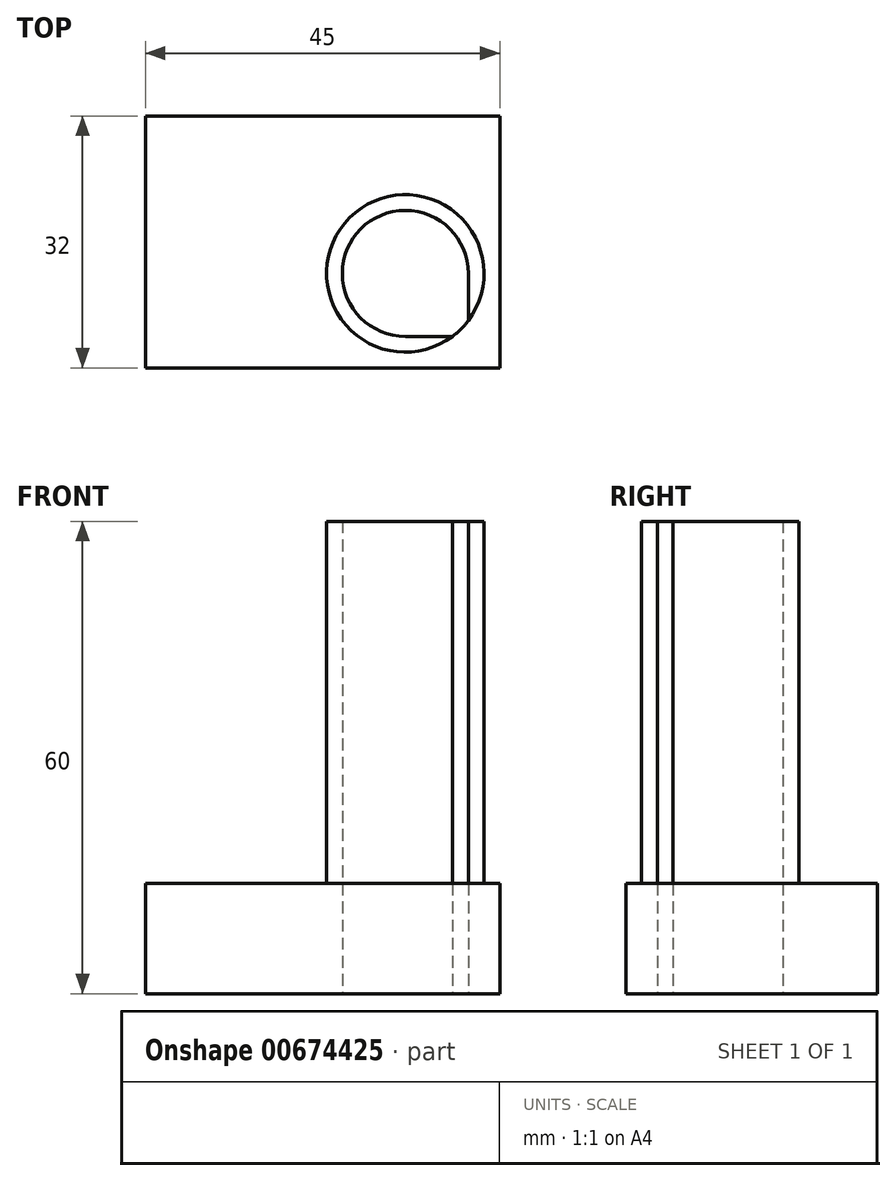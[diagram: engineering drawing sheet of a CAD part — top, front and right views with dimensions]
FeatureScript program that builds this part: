
annotation { "Feature Type Name" : "Feature", "Feature Type Description" : "" }
export const myFeature = defineFeature(function(context is Context, id is Id, definition is map)
    precondition{}
    {
        {
            var Q0;
            Q0=qCreatedBy(makeId("Top.planeOp"),FACE);
            var sketch = newSketch(context, id + "F0", { "sketchPlane" : qUnion([Q0])});
            skLineSegment(sketch, "E0.bottom", {"start": v(0, 0) * mm, "end": v(45, 0) * mm});
            skLineSegment(sketch, "E0.top", {"start": v(0, 32) * mm, "end": v(45, 32) * mm});
            skLineSegment(sketch, "E0.left", {"start": v(0, 0) * mm, "end": v(0, 32) * mm});
            skLineSegment(sketch, "E0.right", {"start": v(45, 0) * mm, "end": v(45, 32) * mm});
            skLineSegment(sketch, "E1.0", {"start": v(2, 2) * mm, "end": v(2, 30) * mm});
            skLineSegment(sketch, "E1.1", {"start": v(2, 2) * mm, "end": v(43, 2) * mm});
            skLineSegment(sketch, "E1.2", {"start": v(43, 2) * mm, "end": v(43, 30) * mm});
            skLineSegment(sketch, "E1.3", {"start": v(2, 30) * mm, "end": v(43, 30) * mm});
            skLineSegment(sketch, "E2.0", {"start": v(41, 4) * mm, "end": v(41, 30) * mm});
            skLineSegment(sketch, "E2.1", {"start": v(2, 4) * mm, "end": v(41, 4) * mm});
            skLineSegment(sketch, "E3.0", {"start": v(46, 4) * mm, "end": v(46, 30) * mm});
            skLineSegment(sketch, "E4", {"start": v(33, 4) * mm, "end": v(33, 30) * mm});
            skLineSegment(sketch, "E5", {"start": v(41, 12) * mm, "end": v(2, 12) * mm});
            skCircle(sketch, "E6", {"center": v(33, 12) * mm, "radius": 8 * mm});
            skCircle(sketch, "E7.0", {"center": v(33, 12) * mm, "radius": 10 * mm});
            skLineSegment(sketch, "E8", {"start": v(0, 14) * mm, "end": v(45, 14) * mm});
            skSolve(sketch);
        }
        {
            var Q0;
            Q0=makeQuery(id+"F0.imprint","IMPRINT",FACE,{"disambiguationData":[TD([[makeQuery(id+"F0.imprint","IMPRINT",EDGE,{"derivedFrom":sQuery(id+"F0.wireOp",EDGE,"E0.bottom")}),1.0]])]});
            var Q1;
            {var subQ1=sQuery(id+"F0.wireOp",EDGE,"E1.3");var subQ5=sQuery(id+"F0.wireOp",EDGE,"E1.0");var subQ6=makeQuery(id+"F0.imprint","INTERSECT",VERTEX,{"derivedFrom":[subQ5,subQ1]});Q1=makeQuery(id+"F0.imprint","IMPRINT",FACE,{"disambiguationData":[TD([[makeQuery(id+"F0.imprint","IMPRINT",EDGE,{"disambiguationData":[TD([[subQ6,1.0]])],"derivedFrom":subQ5}),-1.0]])]});}
            var Q2;
            {var subQ0=sQuery(id+"F0.wireOp",EDGE,"E2.0");var subQ1=sQuery(id+"F0.wireOp",EDGE,"E1.3");var subQ2=makeQuery(id+"F0.imprint","INTERSECT",VERTEX,{"derivedFrom":[subQ1,subQ0]});Q2=makeQuery(id+"F0.imprint","IMPRINT",FACE,{"disambiguationData":[TD([[makeQuery(id+"F0.imprint","IMPRINT",EDGE,{"disambiguationData":[TD([[subQ2,1.0]])],"derivedFrom":subQ1}),-1.0]])]});}
            var Q3;
            {var subQ0=sQuery(id+"F0.wireOp",EDGE,"E2.1");var subQ1=sQuery(id+"F0.wireOp",EDGE,"E1.0");var subQ2=makeQuery(id+"F0.imprint","INTERSECT",VERTEX,{"derivedFrom":[subQ1,subQ0]});Q3=makeQuery(id+"F0.imprint","IMPRINT",FACE,{"disambiguationData":[TD([[makeQuery(id+"F0.imprint","IMPRINT",EDGE,{"disambiguationData":[TD([[subQ2,-1.0]])],"derivedFrom":subQ1}),-1.0]])]});}
            var Q4;
            {var subQ4=sQuery(id+"F0.wireOp",EDGE,"E1.1");Q4=makeQuery(id+"F0.imprint","IMPRINT",FACE,{"disambiguationData":[TD([[makeQuery(id+"F0.imprint","IMPRINT",EDGE,{"derivedFrom":subQ4}),1.0]])]});}
            var Q5;
            {var subQ0=sQuery(id+"F0.wireOp",EDGE,"E2.1");var subQ1=sQuery(id+"F0.wireOp",EDGE,"E2.0");var subQ2=makeQuery(id+"F0.imprint","INTERSECT",VERTEX,{"derivedFrom":[subQ1,subQ0]});Q5=makeQuery(id+"F0.imprint","IMPRINT",FACE,{"disambiguationData":[TD([[makeQuery(id+"F0.imprint","IMPRINT",EDGE,{"disambiguationData":[TD([[subQ2,-1.0]])],"derivedFrom":subQ1}),1.0]])]});}
            var Q6;
            {var subQ0=sQuery(id+"F0.wireOp",EDGE,"E6");var subQ5=sQuery(id+"F0.wireOp",EDGE,"E5");var subQ6=makeQuery(id+"F0.imprint","INTERSECT",VERTEX,{"derivedFrom":[subQ5,subQ0]});Q6=makeQuery(id+"F0.imprint","IMPRINT",FACE,{"disambiguationData":[TD([[makeQuery(id+"F0.imprint","IMPRINT",EDGE,{"disambiguationData":[TD([[subQ6,-1.0]])],"derivedFrom":subQ5}),1.0]])]});}
            var Q7;
            {var subQ2=sQuery(id+"F0.wireOp",EDGE,"E7.0");var subQ4=makeQuery(id+"F0.imprint","INTERSECT",VERTEX,{"derivedFrom":[sQuery(id+"F0.wireOp",EDGE,"E1.1"),subQ2]});Q7=makeQuery(id+"F0.imprint","IMPRINT",FACE,{"disambiguationData":[TD([[makeQuery(id+"F0.imprint","IMPRINT",EDGE,{"disambiguationData":[TD([[subQ4,1.0]])],"derivedFrom":subQ2}),1.0]])]});}
            var Q8;
            {var subQ0=sQuery(id+"F0.wireOp",EDGE,"E6");var subQ1=sQuery(id+"F0.wireOp",EDGE,"E4");var subQ2=makeQuery(id+"F0.imprint","INTERSECT",VERTEX,{"derivedFrom":[subQ1,subQ0]});Q8=makeQuery(id+"F0.imprint","IMPRINT",FACE,{"disambiguationData":[TD([[makeQuery(id+"F0.imprint","IMPRINT",EDGE,{"disambiguationData":[TD([[subQ2,-1.0]])],"derivedFrom":subQ1}),1.0]])]});}
            var Q9;
            {var subQ1=sQuery(id+"F0.wireOp",EDGE,"E2.0");var subQ3=sQuery(id+"F0.wireOp",EDGE,"E7.0");var subQ4=makeQuery(id+"F0.imprint","INTERSECT",VERTEX,{"disambiguationData":[OD(0.0)],"derivedFrom":[subQ1,subQ3]});Q9=makeQuery(id+"F0.imprint","IMPRINT",FACE,{"disambiguationData":[TD([[makeQuery(id+"F0.imprint","IMPRINT",EDGE,{"disambiguationData":[TD([[subQ4,1.0]])],"derivedFrom":subQ3}),1.0]])]});}
            var Q10;
            {var subQ0=sQuery(id+"F0.wireOp",EDGE,"E6");var subQ5=sQuery(id+"F0.wireOp",EDGE,"E4");var subQ6=makeQuery(id+"F0.imprint","INTERSECT",VERTEX,{"derivedFrom":[subQ5,subQ0]});Q10=makeQuery(id+"F0.imprint","IMPRINT",FACE,{"disambiguationData":[TD([[makeQuery(id+"F0.imprint","IMPRINT",EDGE,{"disambiguationData":[TD([[subQ6,-1.0]])],"derivedFrom":subQ5}),-1.0]])]});}
            var Q11;
            {var subQ2=sQuery(id+"F0.wireOp",EDGE,"E7.0");var subQ5=makeQuery(id+"F0.imprint","INTERSECT",VERTEX,{"derivedFrom":[sQuery(id+"F0.wireOp",EDGE,"E1.2"),subQ2]});Q11=makeQuery(id+"F0.imprint","IMPRINT",FACE,{"disambiguationData":[TD([[makeQuery(id+"F0.imprint","IMPRINT",EDGE,{"disambiguationData":[TD([[subQ5,-1.0]])],"derivedFrom":subQ2}),1.0]])]});}
            var Q12;
            {var subQ6=sQuery(id+"F0.wireOp",EDGE,"E1.2");var subQ7=sQuery(id+"F0.wireOp",EDGE,"E1.1");var subQ8=makeQuery(id+"F0.imprint","INTERSECT",VERTEX,{"derivedFrom":[subQ7,subQ6]});Q12=makeQuery(id+"F0.imprint","IMPRINT",FACE,{"disambiguationData":[TD([[makeQuery(id+"F0.imprint","IMPRINT",EDGE,{"disambiguationData":[TD([[subQ8,1.0]])],"derivedFrom":subQ7}),1.0]])]});}
            var Q13;
            {var subQ0=sQuery(id+"F0.wireOp",EDGE,"E1.3");var subQ1=sQuery(id+"F0.wireOp",EDGE,"E1.2");var subQ2=makeQuery(id+"F0.imprint","INTERSECT",VERTEX,{"derivedFrom":[subQ1,subQ0]});Q13=makeQuery(id+"F0.imprint","IMPRINT",FACE,{"disambiguationData":[TD([[makeQuery(id+"F0.imprint","IMPRINT",EDGE,{"disambiguationData":[TD([[subQ2,1.0]])],"derivedFrom":subQ1}),1.0]])]});}
            var Q14;
            {var subQ0=sQuery(id+"F0.wireOp",EDGE,"E5");var subQ1=sQuery(id+"F0.wireOp",EDGE,"E1.0");var subQ2=makeQuery(id+"F0.imprint","INTERSECT",VERTEX,{"derivedFrom":[subQ1,subQ0]});Q14=makeQuery(id+"F0.imprint","IMPRINT",FACE,{"disambiguationData":[TD([[makeQuery(id+"F0.imprint","IMPRINT",EDGE,{"disambiguationData":[TD([[subQ2,-1.0]])],"derivedFrom":subQ1}),-1.0]])]});}
            var Q15;
            {var subQ0=sQuery(id+"F0.wireOp",EDGE,"E6");var subQ1=sQuery(id+"F0.wireOp",EDGE,"E5");var subQ2=makeQuery(id+"F0.imprint","INTERSECT",VERTEX,{"derivedFrom":[subQ1,subQ0]});Q15=makeQuery(id+"F0.imprint","IMPRINT",FACE,{"disambiguationData":[TD([[makeQuery(id+"F0.imprint","IMPRINT",EDGE,{"disambiguationData":[TD([[subQ2,-1.0]])],"derivedFrom":subQ1}),-1.0]])]});}
            var Q16;
            {var subQ0=sQuery(id+"F0.wireOp",EDGE,"E8");var subQ1=sQuery(id+"F0.wireOp",EDGE,"E2.0");var subQ2=makeQuery(id+"F0.imprint","INTERSECT",VERTEX,{"derivedFrom":[subQ1,subQ0]});Q16=makeQuery(id+"F0.imprint","IMPRINT",FACE,{"disambiguationData":[TD([[makeQuery(id+"F0.imprint","IMPRINT",EDGE,{"disambiguationData":[TD([[subQ2,-1.0]])],"derivedFrom":subQ1}),-1.0]])]});}
            var Q17;
            {var subQ6=sQuery(id+"F0.wireOp",EDGE,"E0.top");Q17=makeQuery(id+"F0.imprint","IMPRINT",FACE,{"disambiguationData":[TD([[makeQuery(id+"F0.imprint","IMPRINT",EDGE,{"derivedFrom":subQ6}),-1.0]])]});}
            var Q18;
            {var subQ1=sQuery(id+"F0.wireOp",EDGE,"E2.0");var subQ3=sQuery(id+"F0.wireOp",EDGE,"E8");var subQ4=makeQuery(id+"F0.imprint","INTERSECT",VERTEX,{"derivedFrom":[subQ1,subQ3]});Q18=makeQuery(id+"F0.imprint","IMPRINT",FACE,{"disambiguationData":[TD([[makeQuery(id+"F0.imprint","IMPRINT",EDGE,{"disambiguationData":[TD([[subQ4,1.0]])],"derivedFrom":subQ3}),-1.0]])]});}
            var Q19;
            {var subQ0=sQuery(id+"F0.wireOp",EDGE,"E7.0");var subQ1=sQuery(id+"F0.wireOp",EDGE,"E1.2");var subQ2=makeQuery(id+"F0.imprint","INTERSECT",VERTEX,{"derivedFrom":[subQ1,subQ0]});Q19=makeQuery(id+"F0.imprint","IMPRINT",FACE,{"disambiguationData":[TD([[makeQuery(id+"F0.imprint","IMPRINT",EDGE,{"disambiguationData":[TD([[subQ2,-1.0]])],"derivedFrom":subQ1}),1.0]])]});}
            extrude(context, id + "F1", {"entities" : qUnion([Q0, Q1, Q2, Q3, Q4, Q5, Q6, Q7, Q8, Q9, Q10, Q11, Q12, Q13, Q14, Q15, Q16, Q17, Q18, Q19]), "depth" : 14 * mm, "offsetDistance" : 25 * mm});
        }
        {
            var Q0;
            {var subQ0=sQuery(id+"F0.wireOp",EDGE,"E6");var subQ5=sQuery(id+"F0.wireOp",EDGE,"E5");var subQ6=makeQuery(id+"F0.imprint","INTERSECT",VERTEX,{"derivedFrom":[subQ5,subQ0]});Q0=makeQuery(id+"F0.imprint","IMPRINT",FACE,{"disambiguationData":[TD([[makeQuery(id+"F0.imprint","IMPRINT",EDGE,{"disambiguationData":[TD([[subQ6,-1.0]])],"derivedFrom":subQ5}),1.0]])]});}
            var Q1;
            {var subQ2=sQuery(id+"F0.wireOp",EDGE,"E7.0");var subQ4=makeQuery(id+"F0.imprint","INTERSECT",VERTEX,{"derivedFrom":[sQuery(id+"F0.wireOp",EDGE,"E1.1"),subQ2]});Q1=makeQuery(id+"F0.imprint","IMPRINT",FACE,{"disambiguationData":[TD([[makeQuery(id+"F0.imprint","IMPRINT",EDGE,{"disambiguationData":[TD([[subQ4,1.0]])],"derivedFrom":subQ2}),1.0]])]});}
            var Q2;
            {var subQ1=sQuery(id+"F0.wireOp",EDGE,"E2.0");var subQ3=sQuery(id+"F0.wireOp",EDGE,"E7.0");var subQ4=makeQuery(id+"F0.imprint","INTERSECT",VERTEX,{"disambiguationData":[OD(0.0)],"derivedFrom":[subQ1,subQ3]});Q2=makeQuery(id+"F0.imprint","IMPRINT",FACE,{"disambiguationData":[TD([[makeQuery(id+"F0.imprint","IMPRINT",EDGE,{"disambiguationData":[TD([[subQ4,1.0]])],"derivedFrom":subQ3}),1.0]])]});}
            var Q3;
            {var subQ0=sQuery(id+"F0.wireOp",EDGE,"E7.0");var subQ1=makeQuery(id+"F0.imprint","INTERSECT",VERTEX,{"derivedFrom":[sQuery(id+"F0.wireOp",EDGE,"E1.2"),subQ0]});Q3=makeQuery(id+"F0.imprint","IMPRINT",FACE,{"disambiguationData":[TD([[makeQuery(id+"F0.imprint","IMPRINT",EDGE,{"disambiguationData":[TD([[subQ1,-1.0]])],"derivedFrom":subQ0}),1.0]])]});}
            var Q4;
            {var subQ0=sQuery(id+"F0.wireOp",EDGE,"E6");var subQ1=sQuery(id+"F0.wireOp",EDGE,"E5");var subQ2=makeQuery(id+"F0.imprint","INTERSECT",VERTEX,{"derivedFrom":[subQ1,subQ0]});Q4=makeQuery(id+"F0.imprint","IMPRINT",FACE,{"disambiguationData":[TD([[makeQuery(id+"F0.imprint","IMPRINT",EDGE,{"disambiguationData":[TD([[subQ2,-1.0]])],"derivedFrom":subQ1}),-1.0]])]});}
            var Q5;
            {var subQ0=sQuery(id+"F0.wireOp",EDGE,"E6");var subQ1=sQuery(id+"F0.wireOp",EDGE,"E4");var subQ2=makeQuery(id+"F0.imprint","INTERSECT",VERTEX,{"derivedFrom":[subQ1,subQ0]});Q5=makeQuery(id+"F0.imprint","IMPRINT",FACE,{"disambiguationData":[TD([[makeQuery(id+"F0.imprint","IMPRINT",EDGE,{"disambiguationData":[TD([[subQ2,-1.0]])],"derivedFrom":subQ1}),1.0]])]});}
            var Q6;
            {var subQ1=sQuery(id+"F0.wireOp",EDGE,"E2.0");var subQ7=sQuery(id+"F0.wireOp",EDGE,"E8");var subQ9=makeQuery(id+"F0.imprint","INTERSECT",VERTEX,{"derivedFrom":[subQ1,subQ7]});Q6=makeQuery(id+"F0.imprint","IMPRINT",FACE,{"disambiguationData":[TD([[makeQuery(id+"F0.imprint","IMPRINT",EDGE,{"disambiguationData":[TD([[subQ9,-1.0]])],"derivedFrom":subQ1}),1.0]])]});}
            var Q7;
            {var subQ0=sQuery(id+"F0.wireOp",EDGE,"E8");var subQ1=sQuery(id+"F0.wireOp",EDGE,"E2.0");var subQ2=makeQuery(id+"F0.imprint","INTERSECT",VERTEX,{"derivedFrom":[subQ1,subQ0]});Q7=makeQuery(id+"F0.imprint","IMPRINT",FACE,{"disambiguationData":[TD([[makeQuery(id+"F0.imprint","IMPRINT",EDGE,{"disambiguationData":[TD([[subQ2,-1.0]])],"derivedFrom":subQ1}),-1.0]])]});}
            var Q8;
            {var subQ1=sQuery(id+"F0.wireOp",EDGE,"E2.0");var subQ3=sQuery(id+"F0.wireOp",EDGE,"E8");var subQ4=makeQuery(id+"F0.imprint","INTERSECT",VERTEX,{"derivedFrom":[subQ1,subQ3]});Q8=makeQuery(id+"F0.imprint","IMPRINT",FACE,{"disambiguationData":[TD([[makeQuery(id+"F0.imprint","IMPRINT",EDGE,{"disambiguationData":[TD([[subQ4,1.0]])],"derivedFrom":subQ3}),-1.0]])]});}
            var Q9;
            Q9=sQuery(id+"F0.wireOp",EDGE,"E7.0");
            var Q10;
            Q10=sQuery(id+"F0.wireOp",EDGE,"E6");
            extrude(context, id + "F2", {"entities" : qUnion([Q0, Q1, Q2, Q3, Q4, Q5, Q6, Q7, Q8]), "operationType" : NewBodyOperationType.ADD, "surfaceEntities" : qUnion([Q9, Q10]), "depth" : 60 * mm, "offsetDistance" : 25 * mm});
        }
    });
